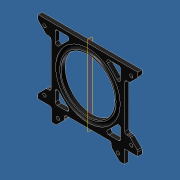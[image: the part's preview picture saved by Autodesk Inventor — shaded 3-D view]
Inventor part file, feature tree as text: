
AUTODESK INVENTOR PART (.ipt)
format: ipt  version: unknown  size: 454,144 bytes
history: native  units: in
note: dims shown in document units (in); Inventor stores cm internally (conversion verified against a paired STEP export)
features: sketch x8, extrude x6, fillet x3, plane x1, revolve x1, hole x1, chamfer x1
ambient origin geometry x8: Origin, YZ Plane, XZ Plane, XY Plane, X Axis, Y Axis, Z Axis, Center Point
bodies: Solid1 (feature_tree)
feature tree (21):
  extrude  "Extrusion1"  Depth=6.0in
  extrude  "Extrusion2"  Depth=3.2269in
  extrude  "Extrusion3"  Depth=3.0in
  plane  "Work Plane1"
  revolve  "Revolution1"  [1 undecoded]
  extrude  "Extrusion4"  Depth=0.8071in
  hole  "Hole1"  [1 undecoded]
  fillet  "Fillet1"  Radius=0.8071in
  extrude  "Extrusion5"  [1 undecoded]
  fillet  "Fillet2"  Radius=3.625in
  extrude  "Extrusion6"  Depth=0.025in
  chamfer  "Chamfer1"  Angle=90.0deg  [1 undecoded]
  fillet  "Fillet3"  Radius=0.7874in
  sketch  "Sketch1"  dims[d0=6.0in d1=6.0in]
  sketch  "Sketch2"  dims[d2=0.25in d3=0.0in d4=3.2269in]
  sketch  "Sketch3"  dims[d5=3.0in d6=3.0in]
  sketch  "Sketch4"  dims[d7=1.0in d8=0.0in d9=0.8071in]
  sketch  "Sketch5"  dims[d10=0.8071in d11=0.8071in]
  sketch  "Sketch6"  dims[d12=0.8071in d13=0.8071in d14=0.8071in]
  sketch  "Sketch7"  dims[d15=1.0in d16=0.0in d17=-3.0in d19=3.625in]
  sketch  "Sketch9"  dims[d20=0.25in d21=0.025in d22=90.0deg d23=0.7874in d24=0.7874in d25=0.7874in d26=0.7874in d27=0.7874in d28=0.7874in d29=0.7874in d30=0.7874in d32=0.7874in d33=0.7874in d35=1.0in d36=0.0in d37=0.3937in d38=0.3937in d39=0.3937in d40=0.3937in d41=0.3937in d42=0.3937in d43=0.3937in d44=0.3937in d45=0.3937in d46=0.3937in d47=0.3937in d48=0.3937in d49=0.201in d50=0.75in d51=0.385in d52=0.25in d53=0.5635in d54=1.0in d55=0.8108in d56=0.125in d57=0.25in d58=0.25in d59=1.0in d60=1.0in d61=0.25in d62=0.25in d63=1.0in d64=1.0in d65=0.25in d66=0.25in d67=1.0in d68=1.0in d69=0.25in d70=0.25in d71=1.0in d72=1.0in d73=1.0in d74=0.0in d75=0.125in d76=0.8071in d77=0.8071in d78=0.7874in d79=0.7874in d80=0.3937in d81=0.3937in d82=0.3937in d83=0.3937in d84=1.0in d85=0.0in d86=3.0in d87=90.0deg d88=0.5in d89=0.125in d90=45.0deg d91=0.125in]
note: 4 required parameter values undecoded (feature->parameter linkage not recoverable at this tier; creation-order binding heuristic only, values carry confidence <= 0.55)